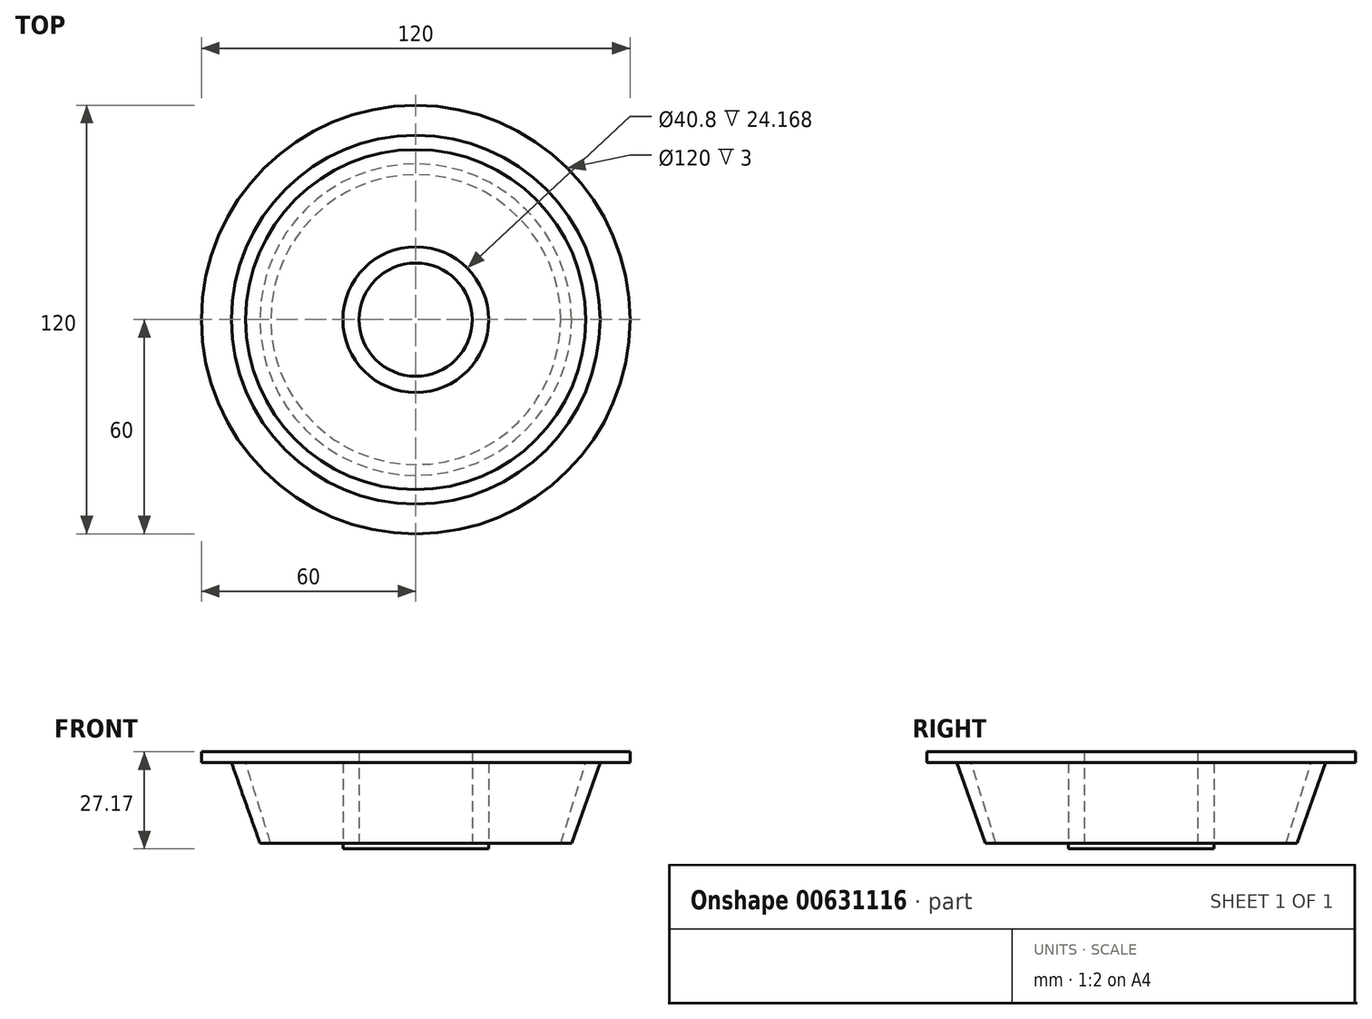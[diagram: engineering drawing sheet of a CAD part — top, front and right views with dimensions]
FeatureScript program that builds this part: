
annotation { "Feature Type Name" : "Feature", "Feature Type Description" : "" }
export const myFeature = defineFeature(function(context is Context, id is Id, definition is map)
    precondition{}
    {
        {
            var Q0;
            Q0=qCreatedBy(makeId("Front.planeOp"),FACE);
            var sketch = newSketch(context, id + "F0", { "sketchPlane" : qUnion([Q0])});
            skLineSegment(sketch, "E0", {"start": v(-15.85, -27.17) * mm, "end": v(-15.85, 0) * mm});
            skLineSegment(sketch, "E1", {"start": v(-15.85, 0) * mm, "end": v(-60, 0) * mm});
            skLineSegment(sketch, "E2", {"start": v(-60, 0) * mm, "end": v(-60, -3) * mm});
            skLineSegment(sketch, "E3", {"start": v(-60, -3) * mm, "end": v(-51.6, -3) * mm});
            skLineSegment(sketch, "E4", {"start": v(-51.6, -3) * mm, "end": v(-43.6, -25.62) * mm});
            skLineSegment(sketch, "E5", {"start": v(-43.6, -25.62) * mm, "end": v(-40.6, -25.62) * mm});
            skLineSegment(sketch, "E6", {"start": v(-40.6, -25.62) * mm, "end": v(-47.6, -3) * mm});
            skLineSegment(sketch, "E7", {"start": v(-47.6, -3) * mm, "end": v(-20.4, -3) * mm});
            skLineSegment(sketch, "E8", {"start": v(-20.4, -3) * mm, "end": v(-20.4, -27.17) * mm});
            skLineSegment(sketch, "E9", {"start": v(-20.4, -27.17) * mm, "end": v(-15.85, -27.17) * mm});
            skLineSegment(sketch, "E10", {"start": v(0, 75.54) * mm, "end": v(0, -75.17) * mm, "construction": true});
            skSolve(sketch);
        }
        {
            var Q0;
            Q0 = qConstructionFilter(qBodyType(qCreatedBy(id + "F0" ,EDGE), BodyType.WIRE), ConstructionObject.NO);
            var Q1;
            Q1=sQuery(id+"F0.wireOp",EDGE,"E10");
            revolve(context, id + "F1", {"bodyType" : ToolBodyType.SURFACE, "surfaceEntities" : qUnion([Q0]), "axis" : qUnion([Q1]), "revolveType" : RevolveType.FULL});
        }
    });
